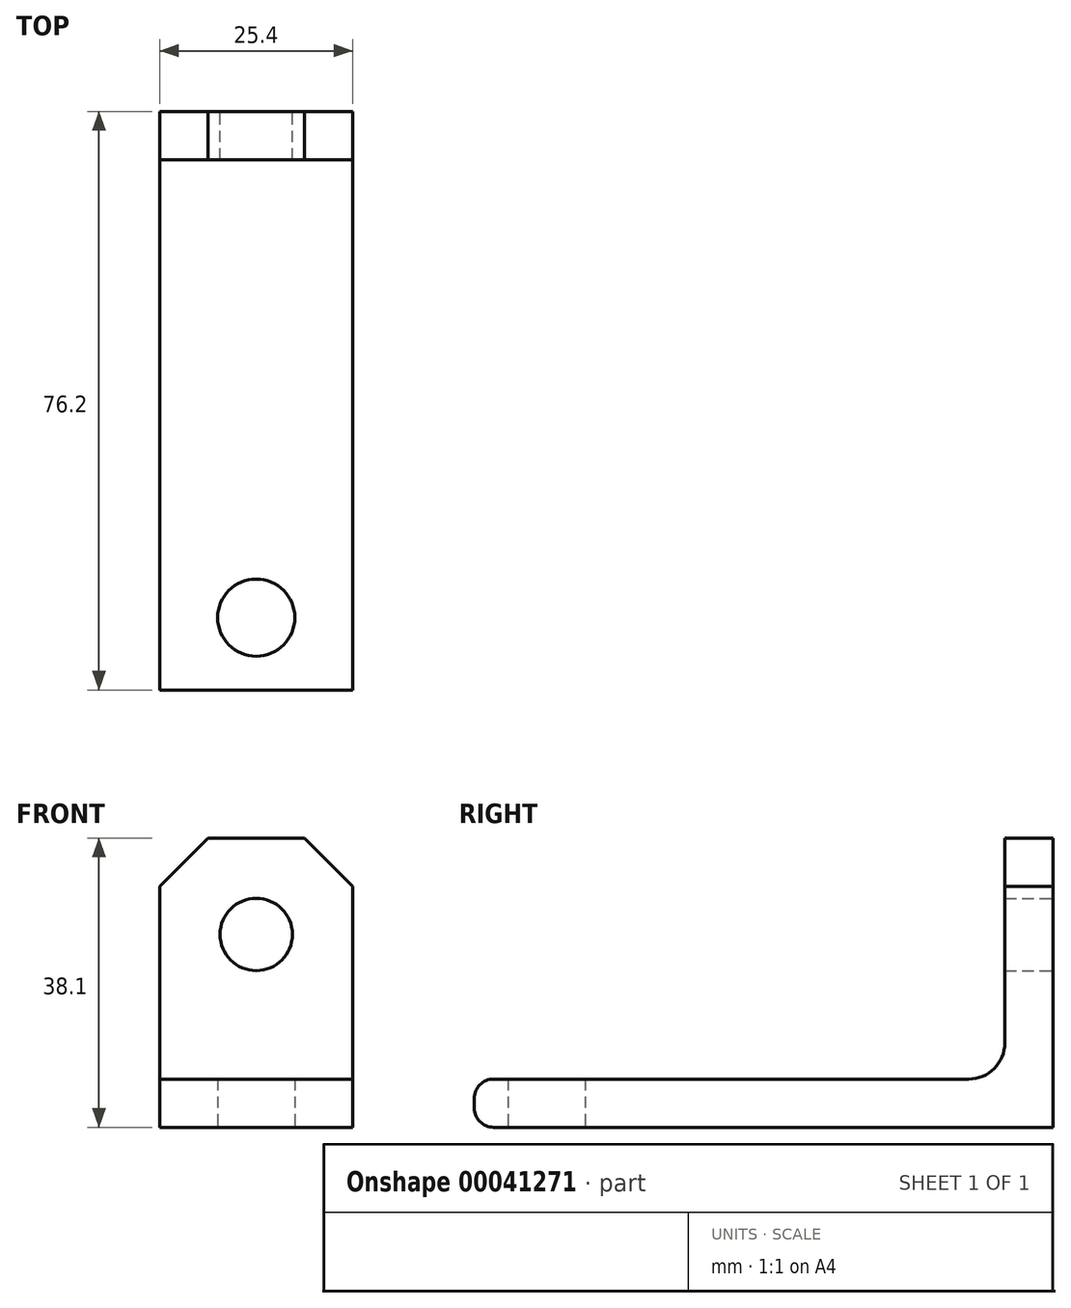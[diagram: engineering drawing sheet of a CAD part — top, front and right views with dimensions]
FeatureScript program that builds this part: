
annotation { "Feature Type Name" : "Feature", "Feature Type Description" : "" }
export const myFeature = defineFeature(function(context is Context, id is Id, definition is map)
    precondition{}
    {
        {
            var Q0;
            Q0=qCreatedBy(makeId("Right.planeOp"),FACE);
            var sketch = newSketch(context, id + "F0", { "sketchPlane" : qUnion([Q0])});
            skLineSegment(sketch, "E0", {"start": v(0, 0) * mm, "end": v(0, 38.1) * mm});
            skLineSegment(sketch, "E1", {"start": v(0, 38.1) * mm, "end": v(-6.35, 38.1) * mm});
            skLineSegment(sketch, "E2", {"start": v(-6.35, 38.1) * mm, "end": v(-6.35, 6.35) * mm});
            skLineSegment(sketch, "E3", {"start": v(-6.35, 6.35) * mm, "end": v(-76.2, 6.35) * mm});
            skLineSegment(sketch, "E4", {"start": v(-76.2, 6.35) * mm, "end": v(-76.2, 0) * mm});
            skLineSegment(sketch, "E5", {"start": v(-76.2, 0) * mm, "end": v(0, 0) * mm});
            skSolve(sketch);
        }
        {
            var Q0;
            Q0=makeQuery(id+"F0.imprint","IMPRINT",FACE,{"disambiguationData":[TD([[makeQuery(id+"F0.imprint","IMPRINT",EDGE,{"derivedFrom":sQuery(id+"F0.wireOp",EDGE,"E0")}),1.0]])]});
            extrude(context, id + "F1", {"entities" : qUnion([Q0]), "depth" : 25.4 * mm});
        }
        {
            var Q0;
            Q0=makeQuery(id+"F1.opExtrude","SWEPT_EDGE",EDGE,{"disambiguationData":[OSD([sQuery(id+"F0.wireOp",EDGE,"E2"),sQuery(id+"F0.wireOp",EDGE,"E3")])]});
            fillet(context, id + "F2", {"entities" : qUnion([Q0]), "radius" : 4.78 * mm, "tangentPropagation" : true, "allowEdgeOverflow" : false});
        }
        {
            var Q0;
            Q0=makeQuery(id+"F1.opExtrude","SWEPT_FACE",FACE,{"disambiguationData":[OSD([sQuery(id+"F0.wireOp",EDGE,"E0")])]});
            var sketch = newSketch(context, id + "F3", { "sketchPlane" : qUnion([Q0])});
            skCircle(sketch, "E6", {"center": v(-12.7, 25.4) * mm, "radius": 4.76 * mm});
            skPoint(sketch, "E6.centerSnap0", {"position": v(-12.7, 0) * mm});
            skSolve(sketch);
        }
        {
            var Q0;
            Q0=makeQuery(id+"F3.imprint","IMPRINT",FACE,{"disambiguationData":[TD([[makeQuery(id+"F3.imprint","IMPRINT",EDGE,{"derivedFrom":sQuery(id+"F3.wireOp",EDGE,"E6")}),1.0]])]});
            extrude(context, id + "F4", {"entities" : qUnion([Q0]), "operationType" : NewBodyOperationType.REMOVE, "oppositeDirection" : true, "depth" : 25.4 * mm});
        }
        {
            var Q0;
            Q0=makeQuery(id+"F1.opExtrude","CAP_EDGE",EDGE,{"disambiguationData":[OSD([sQuery(id+"F0.wireOp",EDGE,"E1")])],"isStart":false});
            var Q1;
            Q1=makeQuery(id+"F1.opExtrude","CAP_EDGE",EDGE,{"disambiguationData":[OSD([sQuery(id+"F0.wireOp",EDGE,"E1")])],"isStart":true});
            chamfer(context, id + "F5", {"entities" : qUnion([Q0, Q1]), "width" : 6.35 * mm, "tangentPropagation" : true});
        }
        {
            var Q0;
            Q0=makeQuery(id+"F1.opExtrude","SWEPT_FACE",FACE,{"disambiguationData":[OSD([sQuery(id+"F0.wireOp",EDGE,"E5")])]});
            var sketch = newSketch(context, id + "F6", { "sketchPlane" : qUnion([Q0])});
            skLineSegment(sketch, "E7", {"start": v(12.7, 0) * mm, "end": v(12.7, 66.68) * mm, "construction": true});
            skCircle(sketch, "E8", {"center": v(12.7, 66.68) * mm, "radius": 5.08 * mm});
            skSolve(sketch);
        }
        {
            var Q0;
            Q0 = qSketchRegion(id + "F6", true);
            extrude(context, id + "F7", {"entities" : qUnion([Q0]), "operationType" : NewBodyOperationType.REMOVE, "oppositeDirection" : true, "depth" : 25.4 * mm});
        }
        {
            var Q0;
            Q0=makeQuery(id+"F1.opExtrude","SWEPT_EDGE",EDGE,{"disambiguationData":[OSD([sQuery(id+"F0.wireOp",EDGE,"E4"),sQuery(id+"F0.wireOp",EDGE,"E5")])]});
            var Q1;
            Q1=makeQuery(id+"F1.opExtrude","SWEPT_EDGE",EDGE,{"disambiguationData":[OSD([sQuery(id+"F0.wireOp",EDGE,"E3"),sQuery(id+"F0.wireOp",EDGE,"E4")])]});
            fillet(context, id + "F8", {"entities" : qUnion([Q0, Q1]), "radius" : 2.54 * mm, "tangentPropagation" : true, "allowEdgeOverflow" : false});
        }
    });
